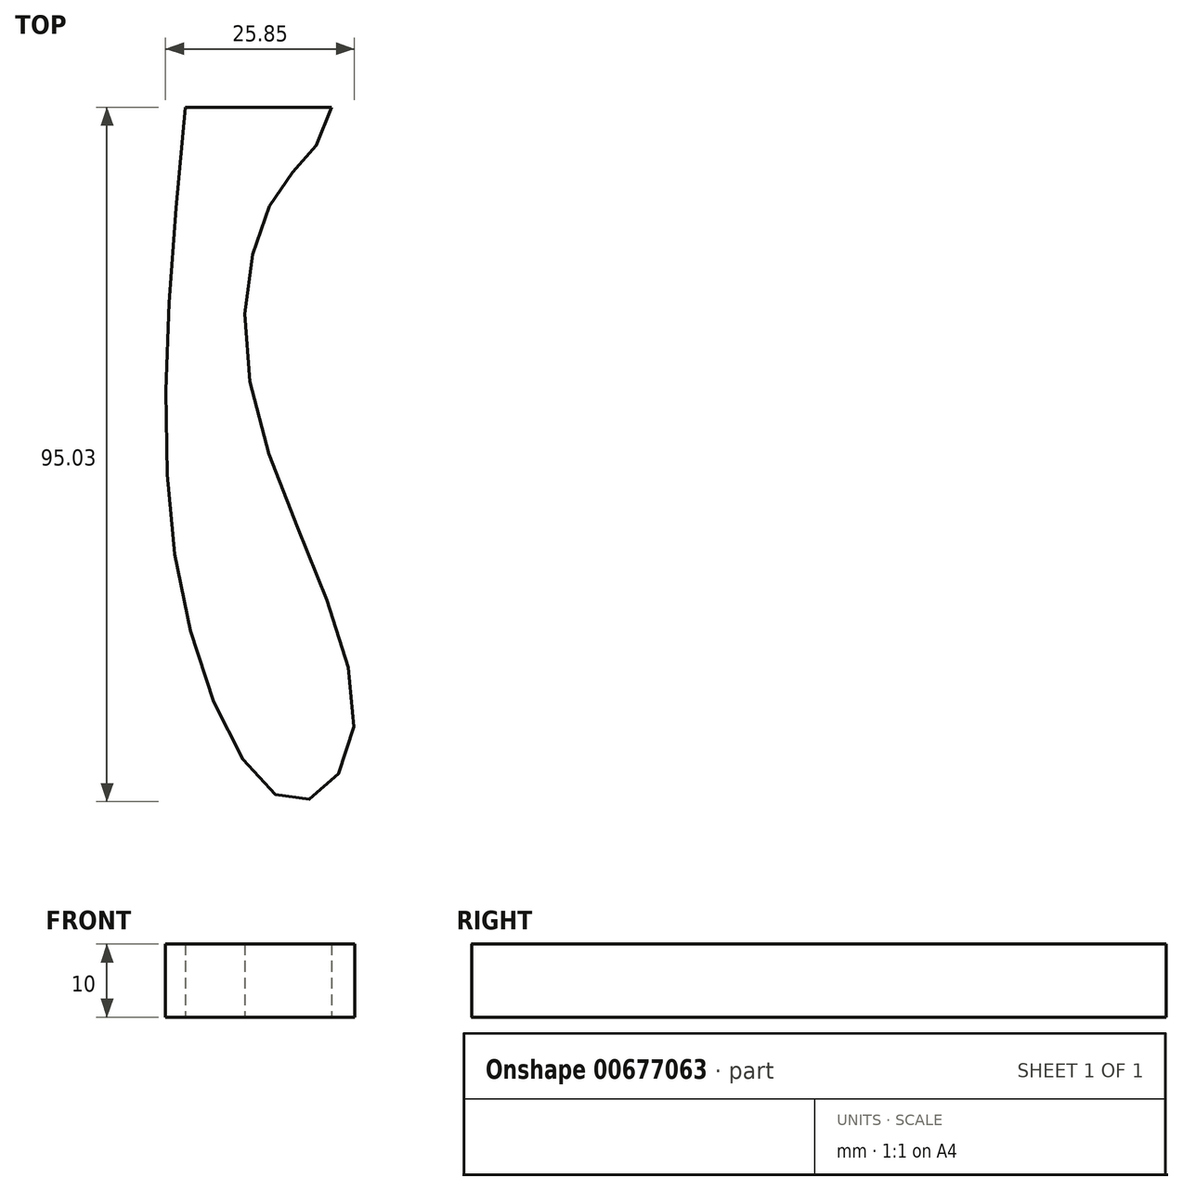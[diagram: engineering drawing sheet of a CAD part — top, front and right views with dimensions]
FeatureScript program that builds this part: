
annotation { "Feature Type Name" : "Feature", "Feature Type Description" : "" }
export const myFeature = defineFeature(function(context is Context, id is Id, definition is map)
    precondition{}
    {
        {
            var Q0;
            Q0=qCreatedBy(makeId("Top.planeOp"),FACE);
            var sketch = newSketch(context, id + "F0", { "sketchPlane" : qUnion([Q0])});
            skFitSpline(sketch, "E0", {"points": [v(0, 0) * mm, v(0, -68.95) * mm, v(14.74, -95) * mm, v(23.1, -84.24) * mm, v(9.16, -39.5) * mm, v(13.07, -10.89) * mm, v(20, 0) * mm], "startDerivative": vector(-30.81, -329.67) * mm, "endDerivative": vector(25.87, 159.04) * mm});
            skLineSegment(sketch, "E1", {"start": v(0, 0) * mm, "end": v(20, 0) * mm});
            skSolve(sketch);
        }
        {
            var Q0;
            Q0=makeQuery(id+"F0.imprint","IMPRINT",FACE,{"disambiguationData":[TD([[makeQuery(id+"F0.imprint","IMPRINT",EDGE,{"derivedFrom":sQuery(id+"F0.wireOp",EDGE,"E0")}),1.0]])]});
            extrude(context, id + "F1", {"entities" : qUnion([Q0]), "depth" : 10 * mm, "offsetDistance" : 25 * mm});
        }
    });
